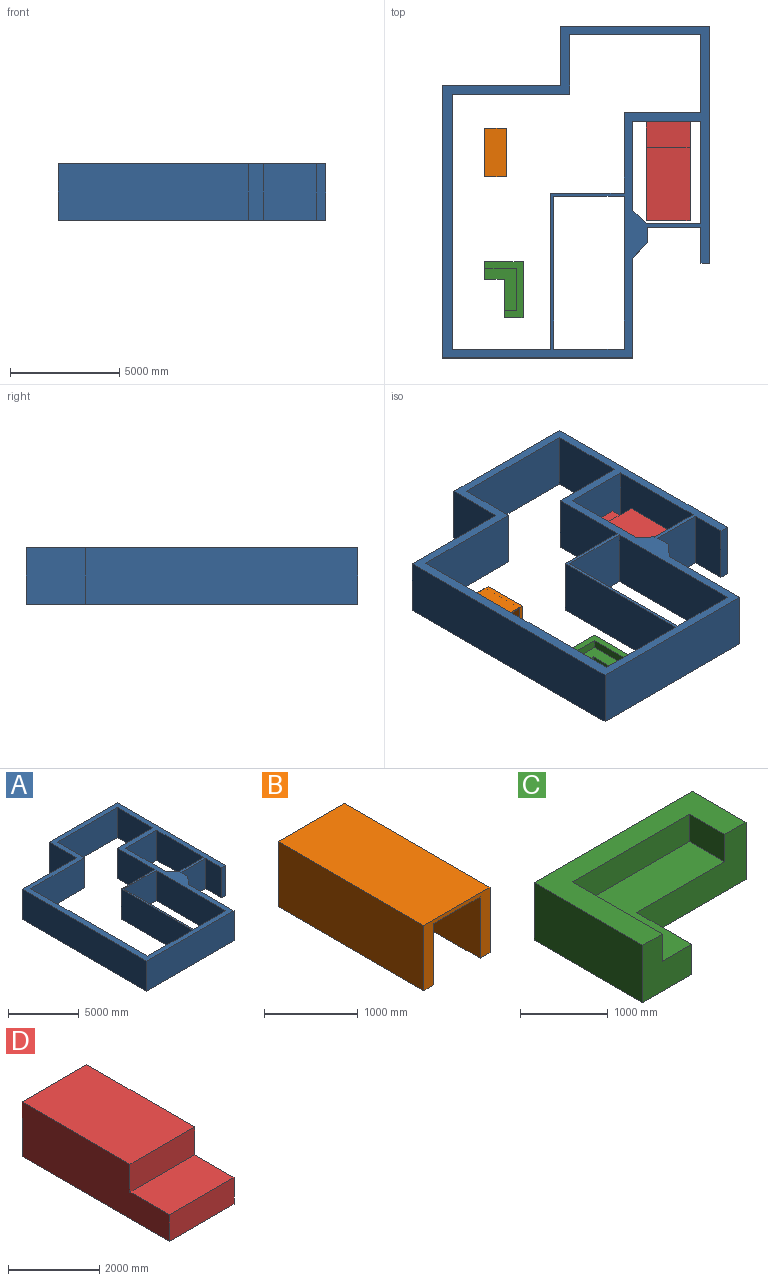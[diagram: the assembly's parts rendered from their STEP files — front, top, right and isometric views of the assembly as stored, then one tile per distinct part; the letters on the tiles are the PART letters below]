
ASSEMBLY  parts=4 mates=4
PART A: 33 faces, bbox 12226.2x15170x2600 mm
  f0: plane 3211.87x2600mm, normal (0,1,0), area 8350872mm2, adj f1,f30,f31,f32
  f1: plane 6984.27x2600mm, normal (1,0,0), area 18159102.9mm2, adj f0,f2,f31,f32
  f2: plane 3211.87x2600mm, normal (0,-1,0), area 8350872mm2, adj f1,f30,f31,f32
  f3: plane 6002.03x2600mm, normal (0,-1,0), area 15605267.2mm2, adj f4,f27,f31,f32
  f4: plane 3550.83x2600mm, normal (-1,0,0), area 9232160mm2, adj f3,f5,f31,f32
  f5: plane 3516.24x2600mm, normal (0,1,0), area 9142225.2mm2, adj f4,f6,f31,f32
  f6: plane 3688.08x2600mm, normal (-1,0,0), area 9589007.4mm2, adj f5,f7,f31,f32
  f7: plane 3352.59x2600mm, normal (0,1,0), area 8716726.4mm2, adj f6,f8,f31,f32
  f8: plane 7131.09x2600mm, normal (-1,0,0), area 18540832.6mm2, adj f7,f9,f31,f32
  f9: plane 4482.48x2600mm, normal (0,1,0), area 11654446.9mm2, adj f8,f10,f31,f32
  f10: plane 11660x2600mm, normal (1,0,0), area 30316000mm2, adj f9,f11,f31,f32
  f11: plane 5349.28x2600mm, normal (0,-1,0), area 13908131.3mm2, adj f10,f27,f31,f32
  f12: plane 10840x2600mm, normal (1,0,0), area 28184000mm2, adj f13,f28,f31,f32
  f13: plane 6820x2600mm, normal (0,1,0), area 17732000mm2, adj f12,f14,f31,f32
  f14: plane 2710x2600mm, normal (-1,0,0), area 7046000mm2, adj f13,f15,f31,f32
  f15: plane 5406.24x2600mm, normal (0,1,0), area 14056225.2mm2, adj f14,f16,f31,f32
  f16: plane 12460x2600mm, normal (-1,0,0), area 32396000mm2, adj f15,f17,f31,f32
  f17: plane 8710x2600mm, normal (0,-1,0), area 22646000mm2, adj f16,f18,f31,f32
  f18: plane 4560.8x2600mm, normal (1,0,0), area 11858070mm2, adj f17,f19,f31,f32
  f19: plane 2600x705.94mm, normal (0.73,-0.68,0), area 2512262.7mm2, adj f18,f20,f31,f32
  f20: plane 2600x686.87mm, normal (1,0,0), area 1785848.6mm2, adj f19,f21,f31,f32
  f21: plane 2600x2456.47mm, normal (0,-1,0), area 6386834.3mm2, adj f20,f22,f31,f32
  f22: plane 2600x1623.61mm, normal (-1,0,0), area 4221374.4mm2, adj f21,f28,f31,f32
  f23: plane 3116.24x2600mm, normal (0,-1,0), area 8102225.2mm2, adj f24,f29,f31,f32
  f24: plane 4684.31x2600mm, normal (-1,0,0), area 12179200.4mm2, adj f23,f25,f31,f32
  f25: plane 2600x2494.63mm, normal (0,1,0), area 6486048mm2, adj f24,f26,f31,f32
  f26: plane 2600x621.61mm, normal (0.7,0.71,0), area 2265376.9mm2, adj f25,f29,f31,f32
  f27: plane 2710x2600mm, normal (1,0,0), area 7046000mm2, adj f3,f11,f31,f32
  f28: plane 2600x400mm, normal (0,-1,0), area 1040000mm2, adj f12,f22,f31,f32
  f29: plane 4073.76x2600mm, normal (1,0,0), area 10591779.9mm2, adj f23,f26,f31,f32
  f30: plane 6984.27x2600mm, normal (-1,0,0), area 18159102.9mm2, adj f0,f2,f31,f32
  f31: plane 15170x12226.24mm, normal (0,0,1), area 27710741.6mm2, adj f0,f1,f2,f3,f4,f5,f6,f7
  f32: plane 15170x12226.24mm, normal (0,0,-1), area 27710741.6mm2, adj f0,f1,f2,f3,f4,f5,f6,f7
PART B: 10 faces, bbox 1000x2200x850 mm
  f0: plane 2200x700mm, normal (0,0,-1), area 1540000mm2, adj f4,f5,f6,f8
  f1: plane 2200x1000mm, normal (0,0,1), area 2200000mm2, adj f2,f3,f4,f5
  f2: plane 2200x850mm, normal (-1,0,0), area 1870000mm2, adj f1,f4,f5,f9
  f3: plane 2200x850mm, normal (1,0,0), area 1870000mm2, adj f1,f4,f5,f7
  f4: plane 1000x850mm, normal (0,-1,0), area 290000mm2, adj f0,f1,f2,f3,f6,f7,f8,f9
  f5: plane 1000x850mm, normal (0,1,0), area 290000mm2, adj f0,f1,f2,f3,f6,f7,f8,f9
  f6: plane 2200x800mm, normal (-1,0,0), area 1760000mm2, adj f0,f4,f5,f7
  f7: plane 2200x150mm, normal (0,0,-1), area 330000mm2, adj f3,f4,f5,f6
  f8: plane 2200x800mm, normal (1,0,0), area 1760000mm2, adj f0,f4,f5,f9
  f9: plane 2200x150mm, normal (0,0,-1), area 330000mm2, adj f2,f4,f5,f8
PART C: 12 faces, bbox 2550x1750x800 mm
  f0: plane 2550x1750mm, normal (0,0,1), area 1410997.8mm2, adj f2,f3,f4,f5,f7,f8,f9,f10
  f1: plane 2550x1750mm, normal (0,0,-1), area 2904905.9mm2, adj f2,f3,f4,f5,f6,f7
  f2: plane 800x790.05mm, normal (0,-1,0), area 451951.6mm2, adj f0,f1,f5,f6,f8,f11
  f3: plane 2550x800mm, normal (0,1,0), area 2040000mm2, adj f0,f1,f4,f5
  f4: plane 864.98x800mm, normal (1,0,0), area 691983.1mm2, adj f0,f1,f3,f7
  f5: plane 1750x800mm, normal (-1,0,0), area 1400000mm2, adj f0,f1,f2,f3
  f6: plane 885.02x420mm, normal (1,0,0), area 371708.9mm2, adj f1,f2,f7,f11
  f7: plane 1759.95x800mm, normal (0,-1,0), area 869127.6mm2, adj f0,f1,f4,f6,f9,f11
  f8: plane 1452.96x380mm, normal (1,0,0), area 552125.3mm2, adj f0,f2,f10,f11
  f9: plane 567.94x380mm, normal (-1,0,0), area 215817.3mm2, adj f0,f7,f10,f11
  f10: plane 1891.9x380mm, normal (0,-1,0), area 718920.8mm2, adj f0,f8,f9,f11
  f11: plane 1891.9x1452.96mm, normal (0,0,1), area 1493908.1mm2, adj f2,f6,f7,f8,f9,f10
PART D: 8 faces, bbox 2000x4562x1461 mm
  f0: plane 2000x747.29mm, normal (0,-1,0), area 1494587.6mm2, adj f1,f5,f6,f7
  f1: plane 2000x1219.69mm, normal (0,0,1), area 2439387.6mm2, adj f0,f2,f6,f7
  f2: plane 2000x713.71mm, normal (0,-1,0), area 1427412.4mm2, adj f1,f3,f6,f7
  f3: plane 4562x2000mm, normal (0,0,-1), area 9124000mm2, adj f2,f4,f6,f7
  f4: plane 2000x1461mm, normal (0,1,0), area 2922000mm2, adj f3,f5,f6,f7
  f5: plane 3342.31x2000mm, normal (0,0,1), area 6684612.4mm2, adj f0,f4,f6,f7
  f6: plane 4562x1461mm, normal (1,0,0), area 5753612.4mm2, adj f0,f1,f2,f3,f4,f5
  f7: plane 4562x1461mm, normal (-1,0,0), area 5753612.4mm2, adj f0,f1,f2,f3,f4,f5
PLACE A t=(0,0,-2470.92)mm
PLACE B rot(axis=(0,0,-1),180deg) t=(-4043.28,-2264.89,-2470.92)mm
PLACE C rot(axis=(0,0,-1),90deg) t=(-3574.82,-6165.21,-2470.92)mm
PLACE D rot(axis=(0,0,-1),180deg) t=(3854.56,-1979,-2470.92)mm
MATE planar C.f1 <-> A.f32  axis (0,0,-1) through (-3420.95,-7228.4,-2470.92)mm
MATE planar B.f9 <-> A.f32  axis (0,0,-1) through (-3539.15,-64.89,-2470.92)mm
MATE parallel D.f7 <-> A.f24  axis (1,0,0) through (4854.56,-4279.26,-2470.92)mm
MATE planar D.f3 <-> A.f32  axis (0,0,-1) through (3854.56,-1998.26,-2470.92)mm
